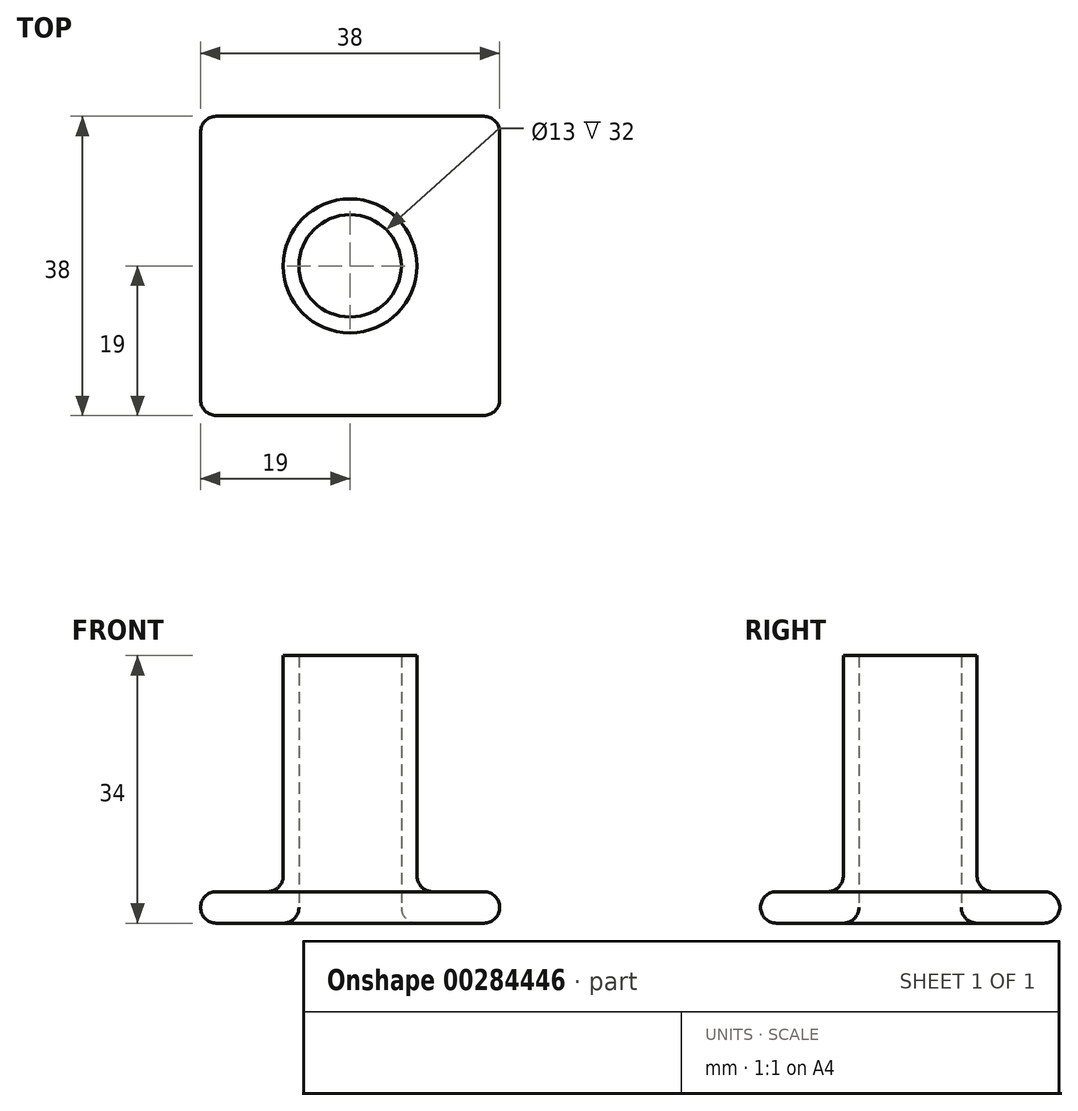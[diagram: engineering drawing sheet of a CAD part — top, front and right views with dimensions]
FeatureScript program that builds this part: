
annotation { "Feature Type Name" : "Feature", "Feature Type Description" : "" }
export const myFeature = defineFeature(function(context is Context, id is Id, definition is map)
    precondition{}
    {
        {
            var Q0;
            Q0=qCreatedBy(makeId("Top.planeOp"),FACE);
            var sketch = newSketch(context, id + "F0", { "sketchPlane" : qUnion([Q0])});
            skCircle(sketch, "E0", {"center": v(0, 0) * mm, "radius": 6.5 * mm});
            skCircle(sketch, "E1", {"center": v(0, 0) * mm, "radius": 8.5 * mm});
            skSolve(sketch);
        }
        {
            var Q0;
            Q0=makeQuery(id+"F0.imprint","IMPRINT",FACE,{"disambiguationData":[TD([[makeQuery(id+"F0.imprint","IMPRINT",EDGE,{"derivedFrom":sQuery(id+"F0.wireOp",EDGE,"E0")}),-1.0]])]});
            extrude(context, id + "F1", {"entities" : qUnion([Q0]), "depth" : 30 * mm});
        }
        {
            var Q0;
            Q0=qCreatedBy(makeId("Top.planeOp"),FACE);
            var sketch = newSketch(context, id + "F2", { "sketchPlane" : qUnion([Q0])});
            skLineSegment(sketch, "E2.bottom", {"start": v(19, -19) * mm, "end": v(-19, -19) * mm});
            skLineSegment(sketch, "E2.top", {"start": v(19, 19) * mm, "end": v(-19, 19) * mm});
            skLineSegment(sketch, "E2.left", {"start": v(19, -19) * mm, "end": v(19, 19) * mm});
            skLineSegment(sketch, "E2.right", {"start": v(-19, -19) * mm, "end": v(-19, 19) * mm});
            skPoint(sketch, "E2.middle", {"position": v(0, 0) * mm});
            skCircle(sketch, "E3", {"center": v(0, 0) * mm, "radius": 6.5 * mm});
            skSolve(sketch);
        }
        {
            var Q0;
            Q0=makeQuery(id+"F2.imprint","IMPRINT",FACE,{"disambiguationData":[TD([[makeQuery(id+"F2.imprint","IMPRINT",EDGE,{"derivedFrom":sQuery(id+"F2.wireOp",EDGE,"E2.bottom")}),-1.0]])]});
            extrude(context, id + "F3", {"entities" : qUnion([Q0]), "operationType" : NewBodyOperationType.ADD, "oppositeDirection" : true, "depth" : 4 * mm});
        }
        {
            var Q0;
            Q0=makeQuery(id+"F3.opExtrude","CAP_FACE",FACE,{"disambiguationData":[OSD([sQuery(id+"F2.wireOp",EDGE,"E2.bottom"),sQuery(id+"F2.wireOp",EDGE,"E2.top"),sQuery(id+"F2.wireOp",EDGE,"E2.left"),sQuery(id+"F2.wireOp",EDGE,"E2.right"),sQuery(id+"F2.wireOp",EDGE,"E3")])],"isStart":false});
            var Q1;
            Q1=makeQuery(id+"F3.opExtrude","CAP_FACE",FACE,{"disambiguationData":[OSD([sQuery(id+"F2.wireOp",EDGE,"E2.bottom"),sQuery(id+"F2.wireOp",EDGE,"E2.top"),sQuery(id+"F2.wireOp",EDGE,"E2.left"),sQuery(id+"F2.wireOp",EDGE,"E2.right"),sQuery(id+"F2.wireOp",EDGE,"E3")])],"isStart":true});
            var Q2;
            Q2=makeQuery(id+"F3.opExtrude","SWEPT_EDGE",EDGE,{"disambiguationData":[OSD([sQuery(id+"F2.wireOp",EDGE,"E2.top"),sQuery(id+"F2.wireOp",EDGE,"E2.left")])]});
            var Q3;
            Q3=makeQuery(id+"F3.opExtrude","SWEPT_EDGE",EDGE,{"disambiguationData":[OSD([sQuery(id+"F2.wireOp",EDGE,"E2.top"),sQuery(id+"F2.wireOp",EDGE,"E2.right")])]});
            var Q4;
            Q4=makeQuery(id+"F3.opExtrude","SWEPT_EDGE",EDGE,{"disambiguationData":[OSD([sQuery(id+"F2.wireOp",EDGE,"E2.bottom"),sQuery(id+"F2.wireOp",EDGE,"E2.left")])]});
            var Q5;
            Q5=makeQuery(id+"F3.opExtrude","SWEPT_EDGE",EDGE,{"disambiguationData":[OSD([sQuery(id+"F2.wireOp",EDGE,"E2.bottom"),sQuery(id+"F2.wireOp",EDGE,"E2.right")])]});
            fillet(context, id + "F4", {"entities" : qUnion([Q0, Q1, Q2, Q3, Q4, Q5]), "radius" : 2 * mm, "tangentPropagation" : true, "allowEdgeOverflow" : false});
        }
    });
